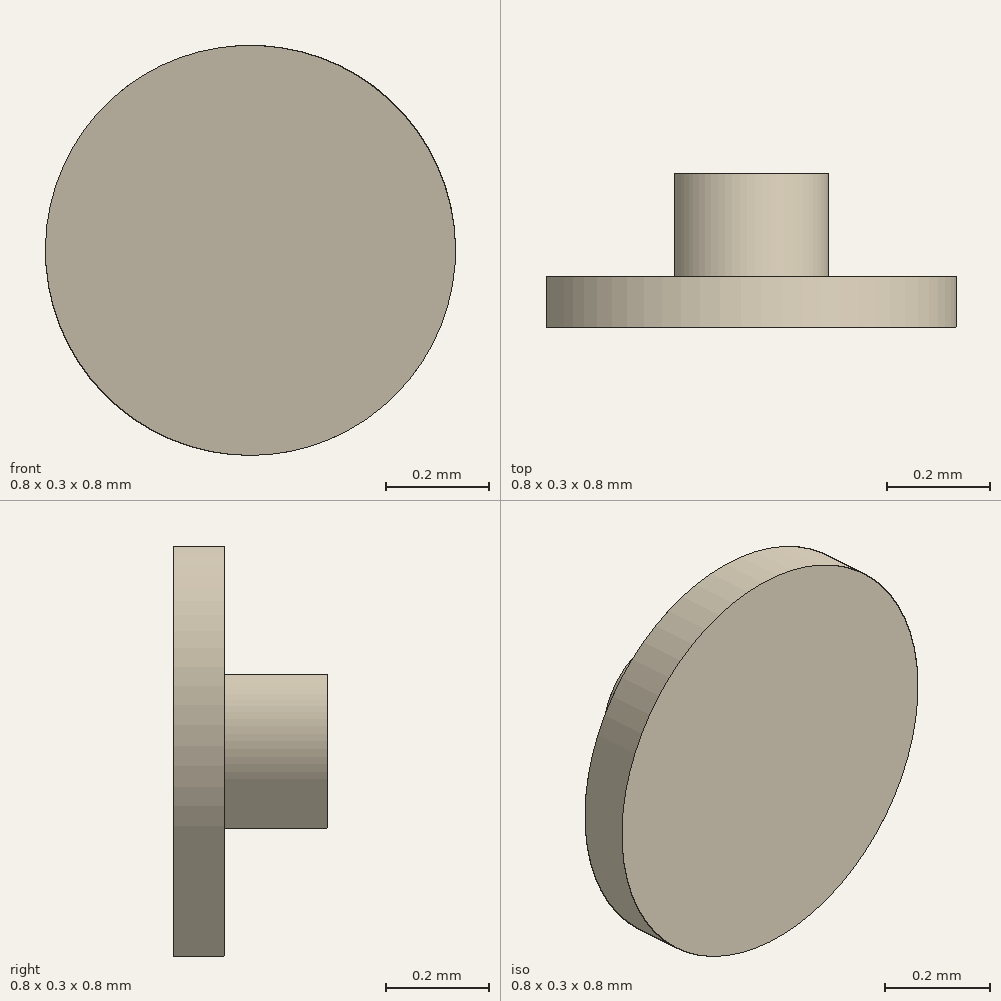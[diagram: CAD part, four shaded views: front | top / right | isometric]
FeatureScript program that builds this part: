
annotation { "Feature Type Name" : "Feature", "Feature Type Description" : "" }
export const myFeature = defineFeature(function(context is Context, id is Id, definition is map)
    precondition{}
    {
        {
            var Q0;
            Q0=qCreatedBy(makeId("Front.planeOp"),FACE);
            var sketch = newSketch(context, id + "F0", { "sketchPlane" : qUnion([Q0])});
            skPoint(sketch, "E0", {"position": v(0, 11.5) * mm});
            skLineSegment(sketch, "E1", {"start": v(0, 11.5) * mm, "end": v(1.75, 11.5) * mm, "construction": true});
            skLineSegment(sketch, "E2", {"start": v(0, 15.23) * mm, "end": v(0, 8.3) * mm, "construction": true});
            skCircle(sketch, "E3", {"center": v(0, 11.5) * mm, "radius": 0.15 * mm});
            skCircle(sketch, "E4", {"center": v(0, 11.5) * mm, "radius": 0.4 * mm});
            skSolve(sketch);
        }
        {
            var Q0;
            Q0=makeQuery(id+"F0.imprint","IMPRINT",FACE,{"disambiguationData":[TD([[makeQuery(id+"F0.imprint","IMPRINT",EDGE,{"derivedFrom":sQuery(id+"F0.wireOp",EDGE,"E3")}),1.0]])]});
            extrude(context, id + "F1", {"entities" : qUnion([Q0]), "oppositeDirection" : true, "depth" : .3 * mm, "offsetDistance" : 25 * mm});
        }
        {
            var Q0;
            Q0=makeQuery(id+"F0.imprint","IMPRINT",FACE,{"disambiguationData":[TD([[makeQuery(id+"F0.imprint","IMPRINT",EDGE,{"derivedFrom":sQuery(id+"F0.wireOp",EDGE,"E3")}),-1.0]])]});
            extrude(context, id + "F2", {"entities" : qUnion([Q0]), "operationType" : NewBodyOperationType.ADD, "oppositeDirection" : true, "depth" : .1 * mm, "offsetDistance" : 25 * mm});
        }
    });
